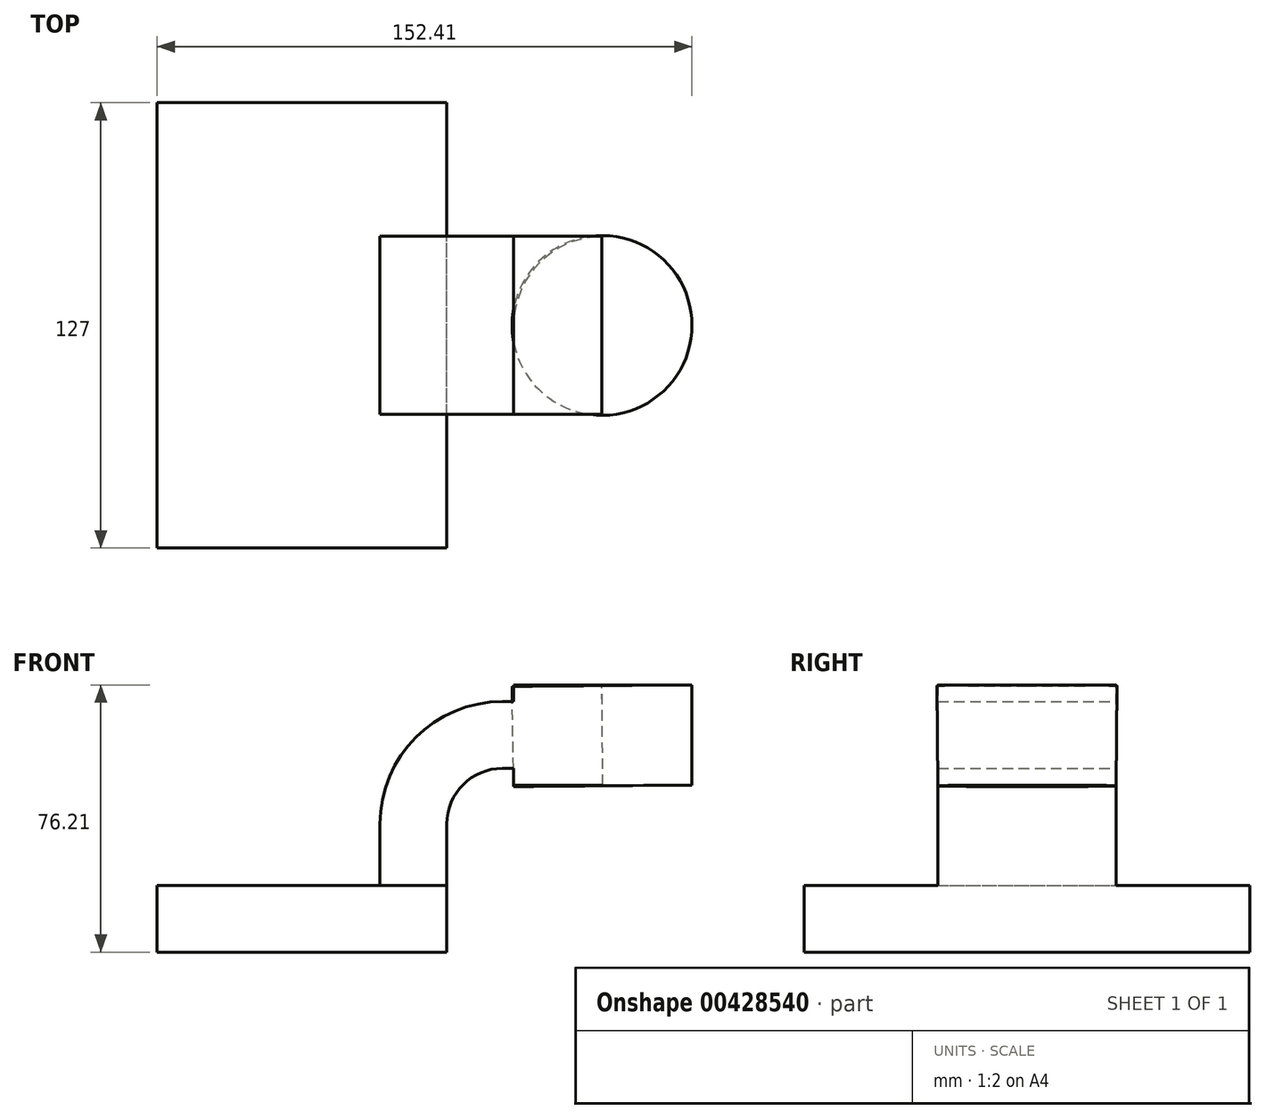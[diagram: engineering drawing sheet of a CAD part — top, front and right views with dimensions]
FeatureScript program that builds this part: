
annotation { "Feature Type Name" : "Feature", "Feature Type Description" : "" }
export const myFeature = defineFeature(function(context is Context, id is Id, definition is map)
    precondition{}
    {
        {
            var Q0;
            Q0=qCreatedBy(makeId("Front.planeOp"),FACE);
            var sketch = newSketch(context, id + "F0", { "sketchPlane" : qUnion([Q0])});
            skLineSegment(sketch, "E0.bottom", {"start": v(-41.28, 9.52) * mm, "end": v(41.27, 9.53) * mm});
            skLineSegment(sketch, "E0.top", {"start": v(-41.28, -9.53) * mm, "end": v(41.28, -9.53) * mm});
            skLineSegment(sketch, "E0.left", {"start": v(-41.28, 9.52) * mm, "end": v(-41.27, -9.53) * mm});
            skLineSegment(sketch, "E0.right", {"start": v(41.28, 9.53) * mm, "end": v(41.28, -9.52) * mm});
            skPoint(sketch, "E0.middle", {"position": v(0, 0) * mm});
            skLineSegment(sketch, "E1.bottom", {"start": v(111.12, 66.68) * mm, "end": v(60.32, 66.68) * mm});
            skLineSegment(sketch, "E1.top", {"start": v(111.12, 38.1) * mm, "end": v(60.32, 38.1) * mm});
            skLineSegment(sketch, "E1.left", {"start": v(111.12, 66.68) * mm, "end": v(111.12, 38.1) * mm});
            skLineSegment(sketch, "E1.right", {"start": v(60.32, 66.68) * mm, "end": v(60.32, 38.1) * mm});
            skPoint(sketch, "E1.middle", {"position": v(85.72, 52.39) * mm});
            skLineSegment(sketch, "E2", {"start": v(41.27, 9.53) * mm, "end": v(41.27, 27) * mm});
            skArc(sketch, "E3", {"start": v(41.27, 27) * mm, "mid": v(45.92, 38.23) * mm, "end": v(57.15, 42.88) * mm});
            skLineSegment(sketch, "E4", {"start": v(57.15, 42.88) * mm, "end": v(85.48, 42.88) * mm});
            skLineSegment(sketch, "E5.0", {"start": v(57.15, 61.93) * mm, "end": v(85.48, 61.93) * mm});
            skArc(sketch, "E5.1", {"start": v(22.22, 27) * mm, "mid": v(32.45, 51.7) * mm, "end": v(57.15, 61.93) * mm});
            skLineSegment(sketch, "E5.2", {"start": v(22.22, 9.53) * mm, "end": v(22.22, 27) * mm});
            skLineSegment(sketch, "E6", {"start": v(85.72, 38.1) * mm, "end": v(85.48, 66.68) * mm});
            skFitSpline(sketch, "E7", {"points": [v(-41.28, 9.52) * mm, v(57.15, 61.93) * mm], "startDerivative": vector(-2.83, 58.89) * mm, "endDerivative": vector(171.45, -2.36) * mm});
            skSolve(sketch);
        }
        {
            var Q0;
            Q0=makeQuery(id+"F0.imprint","IMPRINT",FACE,{"disambiguationData":[TD([[makeQuery(id+"F0.imprint","IMPRINT",EDGE,{"derivedFrom":sQuery(id+"F0.wireOp",EDGE,"E0.top")}),1.0]])]});
            extrude(context, id + "F1", {"entities" : qUnion([Q0]), "endBound" : BoundingType.SYMMETRIC, "depth" : 127 * mm});
        }
        {
            var Q0;
            {var subQ1=sQuery(id+"F0.wireOp",EDGE,"E2");Q0=makeQuery(id+"F0.imprint","IMPRINT",FACE,{"disambiguationData":[TD([[makeQuery(id+"F0.imprint","IMPRINT",EDGE,{"derivedFrom":subQ1}),1.0]])]});}
            var Q1;
            {var subQ6=sQuery(id+"F0.wireOp",EDGE,"E6");Q1=makeQuery(id+"F0.imprint","IMPRINT",FACE,{"disambiguationData":[TD([[makeQuery(id+"F0.imprint","IMPRINT",EDGE,{"derivedFrom":subQ6}),1.0]])]});}
            extrude(context, id + "F2", {"entities" : qUnion([Q0, Q1]), "operationType" : NewBodyOperationType.ADD, "endBound" : BoundingType.SYMMETRIC, "depth" : 50.8 * mm});
        }
        {
            var Q0;
            Q0=makeQuery(id+"F0.imprint","IMPRINT",FACE,{"disambiguationData":[TD([[makeQuery(id+"F0.imprint","IMPRINT",EDGE,{"derivedFrom":sQuery(id+"F0.wireOp",EDGE,"E5.1")}),1.0]])]});
            extrude(context, id + "F3", {"entities" : qUnion([Q0]), "operationType" : NewBodyOperationType.ADD, "endBound" : BoundingType.SYMMETRIC, "depth" : 15.88 * mm});
        }
        {
            var Q0;
            {var subQ0=sQuery(id+"F0.wireOp",EDGE,"E1.left");Q0=makeQuery(id+"F0.imprint","IMPRINT",FACE,{"disambiguationData":[TD([[makeQuery(id+"F0.imprint","IMPRINT",EDGE,{"derivedFrom":subQ0}),-1.0]])]});}
            var Q1;
            Q1=sQuery(id+"F0.wireOp",EDGE,"E6");
            revolve(context, id + "F4", {"entities" : qUnion([Q0]), "axis" : qUnion([Q1]), "revolveType" : RevolveType.FULL, "oppositeDirection" : true});
        }
    });
